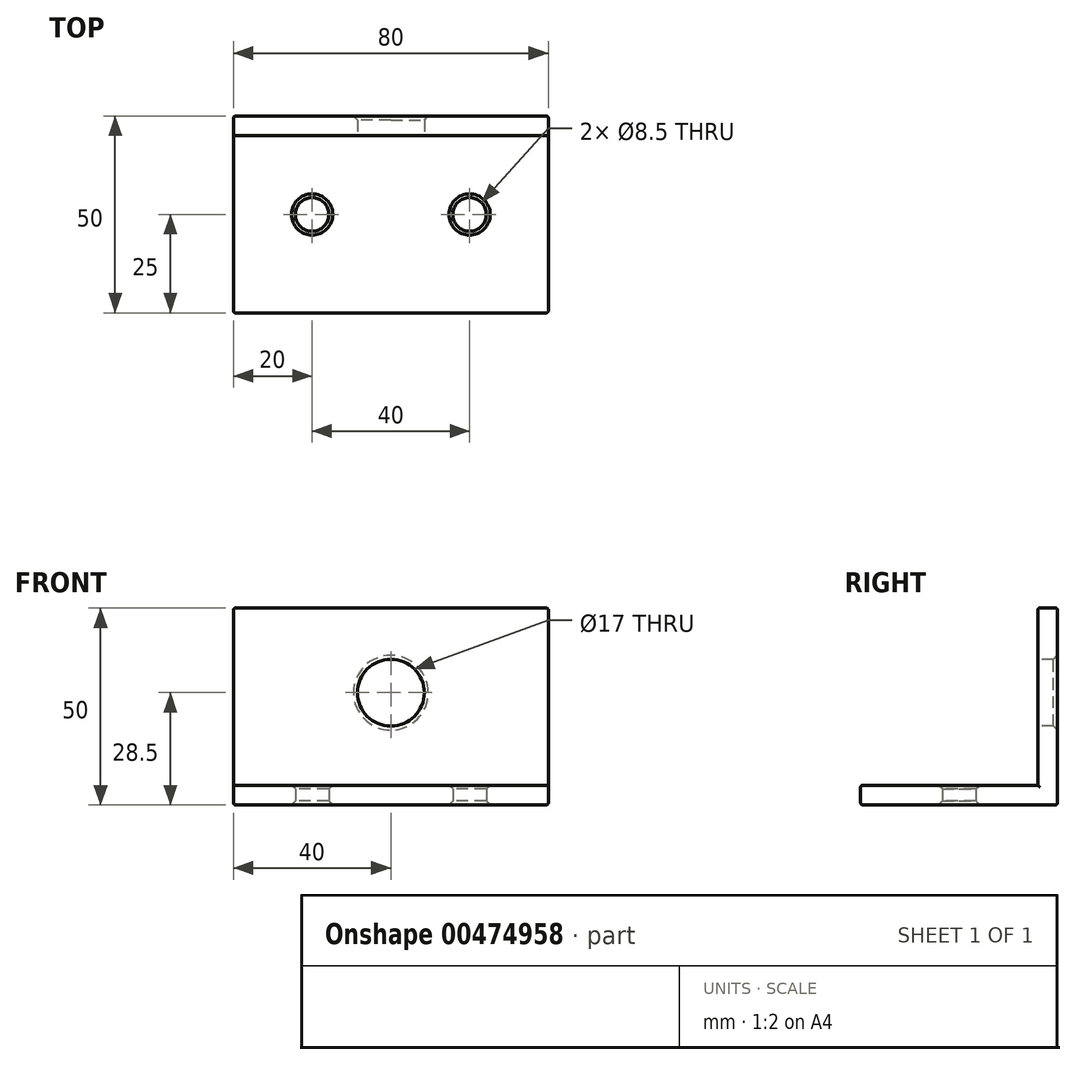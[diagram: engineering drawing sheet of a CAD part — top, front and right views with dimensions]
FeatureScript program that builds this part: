
annotation { "Feature Type Name" : "Feature", "Feature Type Description" : "" }
export const myFeature = defineFeature(function(context is Context, id is Id, definition is map)
    precondition{}
    {
        {
            var Q0;
            Q0=qCreatedBy(makeId("Top.planeOp"),FACE);
            var sketch = newSketch(context, id + "F0", { "sketchPlane" : qUnion([Q0])});
            skLineSegment(sketch, "E0.bottom", {"start": v(0, 0) * mm, "end": v(80, 0) * mm});
            skLineSegment(sketch, "E0.top", {"start": v(0, 50) * mm, "end": v(80, 50) * mm});
            skLineSegment(sketch, "E0.left", {"start": v(0, 0) * mm, "end": v(0, 50) * mm});
            skLineSegment(sketch, "E0.right", {"start": v(80, 0) * mm, "end": v(80, 50) * mm});
            skLineSegment(sketch, "E1", {"start": v(0, 25) * mm, "end": v(80, 25) * mm, "construction": true});
            skCircle(sketch, "E2", {"center": v(20, 25) * mm, "radius": 4.25 * mm});
            skCircle(sketch, "E3", {"center": v(60, 25) * mm, "radius": 4.25 * mm});
            skSolve(sketch);
        }
        {
            var Q0;
            Q0=makeQuery(id+"F0.imprint","IMPRINT",FACE,{"disambiguationData":[TD([[makeQuery(id+"F0.imprint","IMPRINT",EDGE,{"derivedFrom":sQuery(id+"F0.wireOp",EDGE,"E0.bottom")}),1.0]])]});
            extrude(context, id + "F1", {"entities" : qUnion([Q0]), "depth" : 5 * mm});
        }
        {
            var Q0;
            Q0=makeQuery(id+"F1.opExtrude","CAP_FACE",FACE,{"disambiguationData":[OSD([sQuery(id+"F0.wireOp",EDGE,"E0.bottom"),sQuery(id+"F0.wireOp",EDGE,"E0.top"),sQuery(id+"F0.wireOp",EDGE,"E0.left"),sQuery(id+"F0.wireOp",EDGE,"E0.right"),sQuery(id+"F0.wireOp",EDGE,"E2"),sQuery(id+"F0.wireOp",EDGE,"E3")])],"isStart":false});
            var sketch = newSketch(context, id + "F2", { "sketchPlane" : qUnion([Q0])});
            skLineSegment(sketch, "E4.bottom", {"start": v(0, 50) * mm, "end": v(80, 50) * mm});
            skLineSegment(sketch, "E4.top", {"start": v(0, 45) * mm, "end": v(80, 45) * mm});
            skLineSegment(sketch, "E4.left", {"start": v(0, 50) * mm, "end": v(0, 45) * mm});
            skLineSegment(sketch, "E4.right", {"start": v(80, 50) * mm, "end": v(80, 45) * mm});
            skSolve(sketch);
        }
        {
            var Q0;
            Q0=makeQuery(id+"F2.imprint","IMPRINT",FACE,{"disambiguationData":[TD([[makeQuery(id+"F2.imprint","IMPRINT",EDGE,{"derivedFrom":sQuery(id+"F2.wireOp",EDGE,"E4.bottom")}),-1.0]])]});
            extrude(context, id + "F3", {"entities" : qUnion([Q0]), "operationType" : NewBodyOperationType.ADD, "depth" : 45 * mm});
        }
        {
            var Q0;
            Q0=makeQuery(id+"F3.opExtrude","SWEPT_FACE",FACE,{"disambiguationData":[OSD([sQuery(id+"F2.wireOp",EDGE,"E4.top")])]});
            var sketch = newSketch(context, id + "F4", { "sketchPlane" : qUnion([Q0])});
            skLineSegment(sketch, "E5", {"start": v(40, 50) * mm, "end": v(40, 5) * mm, "construction": true});
            skLineSegment(sketch, "E6", {"start": v(0, 28.5) * mm, "end": v(80, 28.5) * mm, "construction": true});
            skCircle(sketch, "E7", {"center": v(40, 28.5) * mm, "radius": 8.5 * mm});
            skSolve(sketch);
        }
        {
            var Q0;
            Q0=makeQuery(id+"F4.imprint","IMPRINT",FACE,{"disambiguationData":[TD([[makeQuery(id+"F4.imprint","IMPRINT",EDGE,{"derivedFrom":sQuery(id+"F4.wireOp",EDGE,"E7")}),1.0]])]});
            extrude(context, id + "F5", {"entities" : qUnion([Q0]), "operationType" : NewBodyOperationType.REMOVE, "oppositeDirection" : true, "depth" : 25 * mm});
        }
        {
            var Q0;
            Q0=makeQuery(id+"F5.boolean.opBoolean","COPY",EDGE,{"derivedFrom":makeQuery(id+"F5.opExtrude","CAP_EDGE",EDGE,{"disambiguationData":[OSD([sQuery(id+"F4.wireOp",EDGE,"E7")])],"isStart":true})});
            var Q1;
            Q1=makeQuery(id+"F5.boolean.opBoolean","INTERSECT",EDGE,{"derivedFrom":[makeQuery(id+"F3.boolean.opBoolean","MERGE",FACE,{"derivedFrom":[makeQuery(id+"F1.opExtrude","SWEPT_FACE",FACE,{"disambiguationData":[OSD([sQuery(id+"F0.wireOp",EDGE,"E0.top")])]}),makeQuery(id+"F3.opExtrude","SWEPT_FACE",FACE,{"disambiguationData":[OSD([sQuery(id+"F2.wireOp",EDGE,"E4.bottom")])]})]}),makeQuery(id+"F5.opExtrude","SWEPT_FACE",FACE,{"disambiguationData":[OSD([sQuery(id+"F4.wireOp",EDGE,"E7")])]})]});
            var Q2;
            Q2=makeQuery(id+"F1.opExtrude","CAP_EDGE",EDGE,{"disambiguationData":[OSD([sQuery(id+"F0.wireOp",EDGE,"E2")])],"isStart":false});
            var Q3;
            Q3=makeQuery(id+"F1.opExtrude","CAP_EDGE",EDGE,{"disambiguationData":[OSD([sQuery(id+"F0.wireOp",EDGE,"E3")])],"isStart":false});
            var Q4;
            Q4=makeQuery(id+"F1.opExtrude","CAP_EDGE",EDGE,{"disambiguationData":[OSD([sQuery(id+"F0.wireOp",EDGE,"E3")])],"isStart":true});
            var Q5;
            Q5=makeQuery(id+"F1.opExtrude","CAP_EDGE",EDGE,{"disambiguationData":[OSD([sQuery(id+"F0.wireOp",EDGE,"E2")])],"isStart":true});
            chamfer(context, id + "F6", {"entities" : qUnion([Q0, Q1, Q2, Q3, Q4, Q5]), "width" : 1 * mm, "tangentPropagation" : true});
        }
        {
            var Q0;
            Q0=makeQuery(id+"F3.opExtrude","CAP_FACE",FACE,{"disambiguationData":[OSD([sQuery(id+"F2.wireOp",EDGE,"E4.bottom"),sQuery(id+"F2.wireOp",EDGE,"E4.top"),sQuery(id+"F2.wireOp",EDGE,"E4.left"),sQuery(id+"F2.wireOp",EDGE,"E4.right")])],"isStart":false});
            var Q1;
            Q1=makeQuery(id+"F3.boolean.opBoolean","MERGE",FACE,{"derivedFrom":[makeQuery(id+"F1.opExtrude","SWEPT_FACE",FACE,{"disambiguationData":[OSD([sQuery(id+"F0.wireOp",EDGE,"E0.left")])]}),makeQuery(id+"F3.opExtrude","SWEPT_FACE",FACE,{"disambiguationData":[OSD([sQuery(id+"F2.wireOp",EDGE,"E4.left")])]})]});
            var Q2;
            Q2=makeQuery(id+"F1.opExtrude","SWEPT_FACE",FACE,{"disambiguationData":[OSD([sQuery(id+"F0.wireOp",EDGE,"E0.bottom")])]});
            var Q3;
            Q3=makeQuery(id+"F1.opExtrude","CAP_EDGE",EDGE,{"disambiguationData":[OSD([sQuery(id+"F0.wireOp",EDGE,"E0.right")])],"isStart":false});
            var Q4;
            Q4=makeQuery(id+"F3.boolean.opBoolean","MERGE",FACE,{"derivedFrom":[makeQuery(id+"F1.opExtrude","SWEPT_FACE",FACE,{"disambiguationData":[OSD([sQuery(id+"F0.wireOp",EDGE,"E0.right")])]}),makeQuery(id+"F3.opExtrude","SWEPT_FACE",FACE,{"disambiguationData":[OSD([sQuery(id+"F2.wireOp",EDGE,"E4.right")])]})]});
            var Q5;
            Q5=makeQuery(id+"F1.opExtrude","CAP_EDGE",EDGE,{"disambiguationData":[OSD([sQuery(id+"F0.wireOp",EDGE,"E0.top")])],"isStart":true});
            fillet(context, id + "F7", {"entities" : qUnion([Q0, Q1, Q2, Q3, Q4, Q5]), "radius" : 0.5 * mm, "tangentPropagation" : true, "allowEdgeOverflow" : false});
        }
    });
